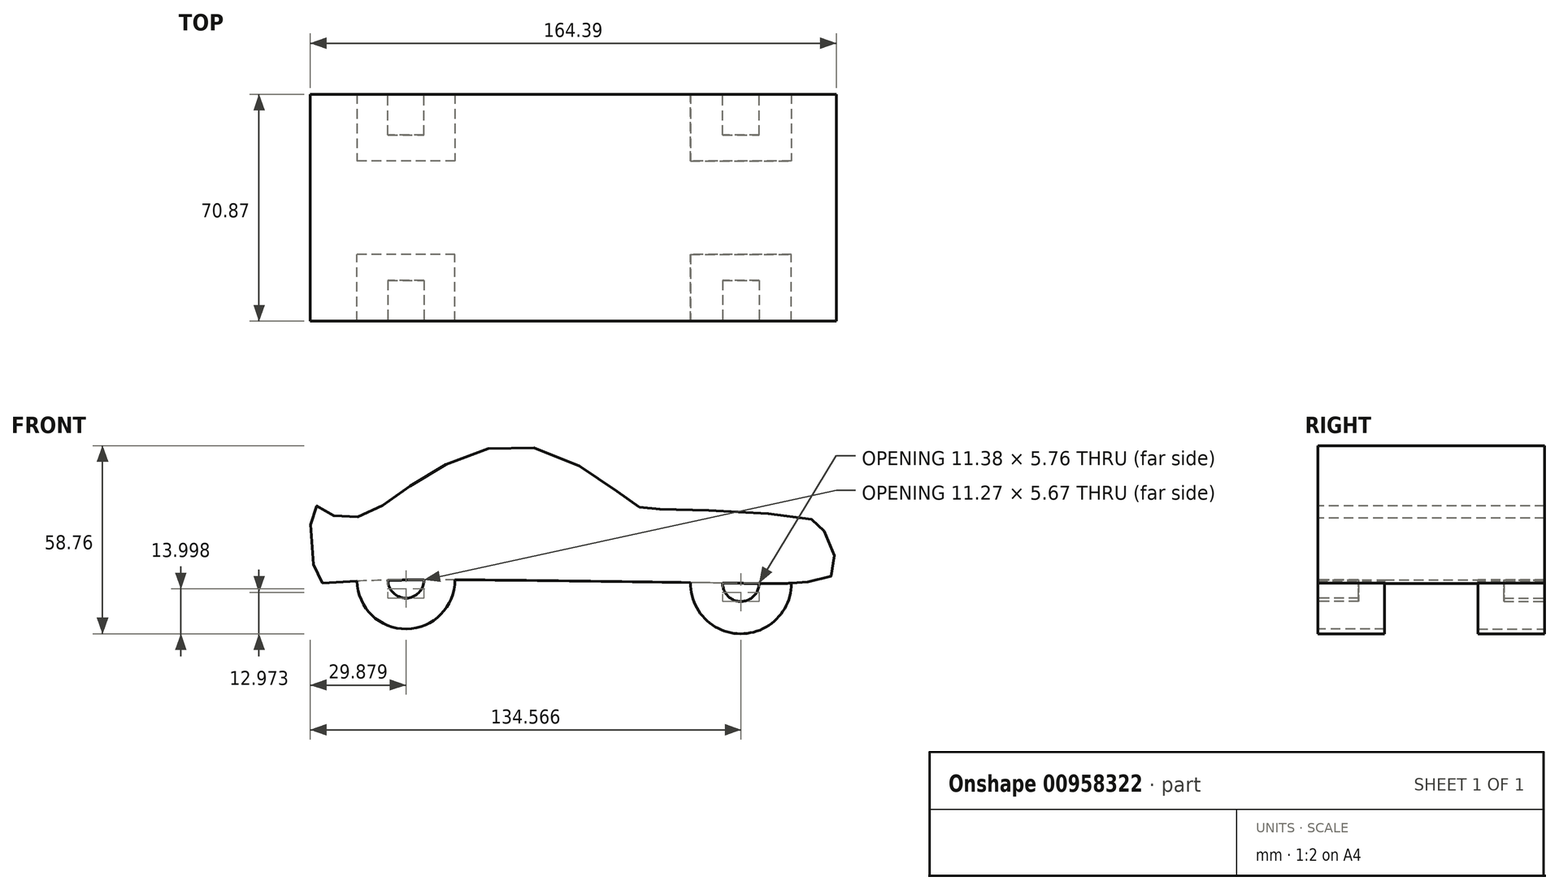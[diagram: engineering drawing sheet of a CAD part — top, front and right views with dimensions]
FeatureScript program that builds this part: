
annotation { "Feature Type Name" : "Feature", "Feature Type Description" : "" }
export const myFeature = defineFeature(function(context is Context, id is Id, definition is map)
    precondition{}
    {
        {
            var Q0;
            Q0=qCreatedBy(makeId("Front.planeOp"),FACE);
            var sketch = newSketch(context, id + "F0", { "sketchPlane" : qUnion([Q0])});
            skFitSpline(sketch, "E0", {"points": [v(-72.57, 26.76) * mm, v(-68.25, 24.85) * mm, v(-57.38, 23.92) * mm, v(-40.44, 34.53) * mm, v(-4.1, 45.23) * mm, v(27.67, 27.57) * mm, v(34.56, 26) * mm, v(83.46, 22.66) * mm, v(87.26, 18.45) * mm, v(90.35, 6.23) * mm, v(80.99, 3.19) * mm, v(73.57, 2.76) * mm, v(-64.11, 3.22) * mm, v(-71.86, 5.07) * mm, v(-72.57, 26.76) * mm]});
            skSolve(sketch);
        }
        {
            var Q0;
            Q0 = qSketchRegion(id + "F0", true);
            extrude(context, id + "F1", {"entities" : qUnion([Q0]), "depth" : 70.87 * mm, "offsetDistance" : 25.4 * mm});
        }
        {
            var Q0;
            Q0=makeQuery(id+"F1.opExtrude","CAP_FACE",FACE,{"disambiguationData":[OSD([sQuery(id+"F0.wireOp",EDGE,"E0")])],"isStart":false});
            var sketch = newSketch(context, id + "F2", { "sketchPlane" : qUnion([Q0])});
            skCircle(sketch, "E1", {"center": v(-43.73, 3.83) * mm, "radius": 15.3 * mm});
            skCircle(sketch, "E2", {"center": v(60.96, 2.81) * mm, "radius": 15.79 * mm});
            skSolve(sketch);
        }
        {
            var Q0;
            {var subQ0=sQuery(id+"F2.wireOp",EDGE,"E1");var subQ1=makeQuery(id+"F1.opExtrude","CAP_EDGE",EDGE,{"disambiguationData":[OSD([sQuery(id+"F0.wireOp",EDGE,"E0")])],"isStart":false});var subQ2=makeQuery(id+"F2.imprint","INTERSECT",VERTEX,{"disambiguationData":[OD(0.0)],"derivedFrom":[subQ1,subQ0]});Q0=makeQuery(id+"F2.imprint","IMPRINT",FACE,{"disambiguationData":[TD([[makeQuery(id+"F2.imprint","IMPRINT",EDGE,{"disambiguationData":[TD([[subQ2,1.0]])],"derivedFrom":subQ0}),1.0]])]});}
            var Q1;
            {var subQ0=sQuery(id+"F2.wireOp",EDGE,"E1");var subQ1=makeQuery(id+"F1.opExtrude","CAP_EDGE",EDGE,{"disambiguationData":[OSD([sQuery(id+"F0.wireOp",EDGE,"E0")])],"isStart":false});var subQ2=makeQuery(id+"F2.imprint","INTERSECT",VERTEX,{"disambiguationData":[OD(0.0)],"derivedFrom":[subQ1,subQ0]});Q1=makeQuery(id+"F2.imprint","IMPRINT",FACE,{"disambiguationData":[TD([[makeQuery(id+"F2.imprint","IMPRINT",EDGE,{"disambiguationData":[TD([[subQ2,-1.0]])],"derivedFrom":subQ0}),1.0]])]});}
            var Q2;
            {var subQ0=sQuery(id+"F2.wireOp",EDGE,"E2");var subQ1=makeQuery(id+"F1.opExtrude","CAP_EDGE",EDGE,{"disambiguationData":[OSD([sQuery(id+"F0.wireOp",EDGE,"E0")])],"isStart":false});var subQ2=makeQuery(id+"F2.imprint","INTERSECT",VERTEX,{"disambiguationData":[OD(0.0)],"derivedFrom":[subQ1,subQ0]});Q2=makeQuery(id+"F2.imprint","IMPRINT",FACE,{"disambiguationData":[TD([[makeQuery(id+"F2.imprint","IMPRINT",EDGE,{"disambiguationData":[TD([[subQ2,1.0]])],"derivedFrom":subQ0}),1.0]])]});}
            var Q3;
            {var subQ0=sQuery(id+"F2.wireOp",EDGE,"E2");var subQ1=makeQuery(id+"F1.opExtrude","CAP_EDGE",EDGE,{"disambiguationData":[OSD([sQuery(id+"F0.wireOp",EDGE,"E0")])],"isStart":false});var subQ2=makeQuery(id+"F2.imprint","INTERSECT",VERTEX,{"disambiguationData":[OD(0.0)],"derivedFrom":[subQ1,subQ0]});Q3=makeQuery(id+"F2.imprint","IMPRINT",FACE,{"disambiguationData":[TD([[makeQuery(id+"F2.imprint","IMPRINT",EDGE,{"disambiguationData":[TD([[subQ2,-1.0]])],"derivedFrom":subQ0}),1.0]])]});}
            extrude(context, id + "F3", {"entities" : qUnion([Q0, Q1, Q2, Q3]), "operationType" : NewBodyOperationType.ADD, "oppositeDirection" : true, "depth" : 20.83 * mm, "offsetDistance" : 25.4 * mm});
        }
        {
            var Q0;
            Q0=makeQuery(id+"F3.boolean.opBoolean","MERGE",FACE,{"derivedFrom":[makeQuery(id+"F1.opExtrude","CAP_FACE",FACE,{"disambiguationData":[OSD([sQuery(id+"F0.wireOp",EDGE,"E0")])],"isStart":false}),makeQuery(id+"F3.opExtrude","CAP_FACE",FACE,{"disambiguationData":[OSD([sQuery(id+"F2.wireOp",EDGE,"E1")])],"isStart":true}),makeQuery(id+"F3.opExtrude","CAP_FACE",FACE,{"disambiguationData":[OSD([sQuery(id+"F2.wireOp",EDGE,"E2")])],"isStart":true})]});
            var sketch = newSketch(context, id + "F4", { "sketchPlane" : qUnion([Q0])});
            skCircle(sketch, "E3", {"center": v(-43.73, 3.83) * mm, "radius": 5.64 * mm});
            skCircle(sketch, "E4", {"center": v(60.96, 2.81) * mm, "radius": 5.7 * mm});
            skSolve(sketch);
        }
        {
            var Q0;
            Q0 = qSketchRegion(id + "F4", true);
            extrude(context, id + "F5", {"entities" : qUnion([Q0]), "operationType" : NewBodyOperationType.REMOVE, "oppositeDirection" : true, "depth" : 12.7 * mm, "offsetDistance" : 25.4 * mm});
        }
        {
            var Q0;
            Q0=makeQuery(id+"F3.boolean.opBoolean","MERGE",FACE,{"derivedFrom":[makeQuery(id+"F1.opExtrude","CAP_FACE",FACE,{"disambiguationData":[OSD([sQuery(id+"F0.wireOp",EDGE,"E0")])],"isStart":false}),makeQuery(id+"F3.opExtrude","CAP_FACE",FACE,{"disambiguationData":[OSD([sQuery(id+"F2.wireOp",EDGE,"E1")])],"isStart":true}),makeQuery(id+"F3.opExtrude","CAP_FACE",FACE,{"disambiguationData":[OSD([sQuery(id+"F2.wireOp",EDGE,"E2")])],"isStart":true})]});
            var Q1;
            Q1=makeQuery(id+"F1.opExtrude","CAP_FACE",FACE,{"disambiguationData":[OSD([sQuery(id+"F0.wireOp",EDGE,"E0")])],"isStart":true});
            cPlane(context, id + "F6", {"entities" : qUnion([Q0, Q1]), "cplaneType" : CPlaneType.MID_PLANE, "offset" : 25.4 * mm, "width" : 152.4 * mm, "height" : 152.4 * mm});
        }
        {
            var Q0;
            Q0=makeQuery(id+"F1.opExtrude","SWEPT_BODY",BODY,{"disambiguationData":[OSD([sQuery(id+"F0.wireOp",EDGE,"E0")])]});
            var Q1;
            Q1=qCreatedBy(id+"F6.planeOp",FACE);
            mirror(context, id + "F7", {"operationType" : NewBodyOperationType.ADD, "entities" : qUnion([Q0]), "mirrorPlane" : qUnion([Q1])});
        }
    });
